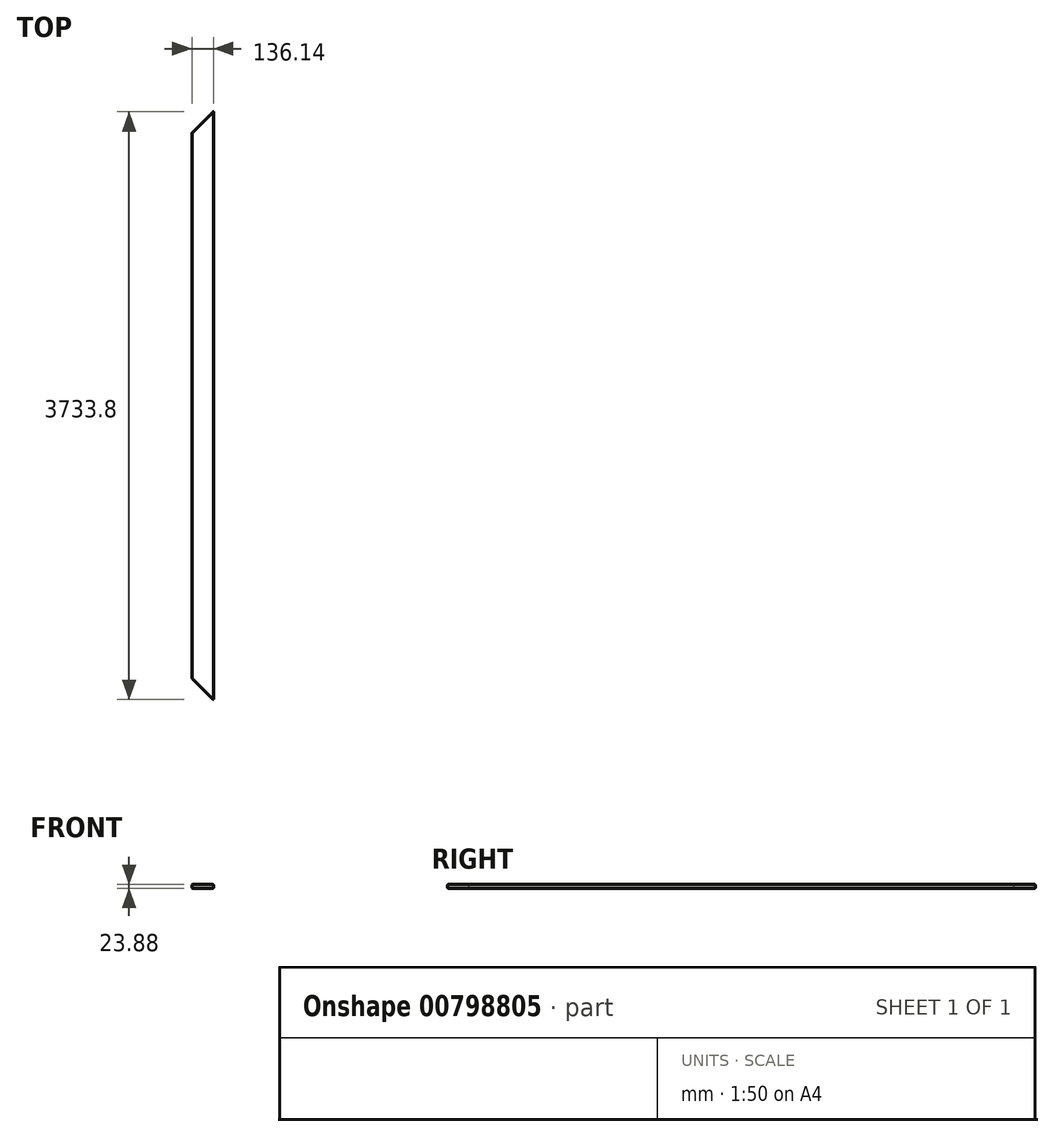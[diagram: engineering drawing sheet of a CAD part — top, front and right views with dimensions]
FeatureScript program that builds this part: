
annotation { "Feature Type Name" : "Feature", "Feature Type Description" : "" }
export const myFeature = defineFeature(function(context is Context, id is Id, definition is map)
    precondition{}
    {
        {
            var Q0;
            Q0=qCreatedBy(makeId("Front.planeOp"),FACE);
            var sketch = newSketch(context, id + "F0", { "sketchPlane" : qUnion([Q0])});
            skLineSegment(sketch, "E0.bottom", {"start": v(-63.25, 11.94) * mm, "end": v(63.25, 11.94) * mm});
            skLineSegment(sketch, "E0.top", {"start": v(-63.25, -11.94) * mm, "end": v(63.25, -11.94) * mm});
            skLineSegment(sketch, "E0.left", {"start": v(-68.07, 7.11) * mm, "end": v(-68.07, -7.11) * mm});
            skLineSegment(sketch, "E0.right", {"start": v(68.07, 7.11) * mm, "end": v(68.07, -7.11) * mm});
            skPoint(sketch, "E0.middle", {"position": v(0, 0) * mm});
            skPoint(sketch, "E1.visualSharp", {"position": v(-68.07, 11.94) * mm});
            skArc(sketch, "E1.filletArc", {"start": v(-63.25, 11.94) * mm, "mid": v(-66.66, 10.52) * mm, "end": v(-68.07, 7.11) * mm});
            skPoint(sketch, "E2.visualSharp", {"position": v(68.07, 11.94) * mm});
            skArc(sketch, "E2.filletArc", {"start": v(68.07, 7.11) * mm, "mid": v(66.66, 10.52) * mm, "end": v(63.25, 11.94) * mm});
            skPoint(sketch, "E3.visualSharp", {"position": v(68.07, -11.94) * mm});
            skArc(sketch, "E3.filletArc", {"start": v(63.25, -11.94) * mm, "mid": v(66.66, -10.52) * mm, "end": v(68.07, -7.11) * mm});
            skPoint(sketch, "E4.visualSharp", {"position": v(-68.07, -11.94) * mm});
            skArc(sketch, "E4.filletArc", {"start": v(-68.07, -7.11) * mm, "mid": v(-66.66, -10.52) * mm, "end": v(-63.25, -11.94) * mm});
            skSolve(sketch);
        }
        {
            var Q0;
            Q0=makeQuery(id+"F0.imprint","IMPRINT",FACE,{"disambiguationData":[TD([[makeQuery(id+"F0.imprint","IMPRINT",EDGE,{"derivedFrom":sQuery(id+"F0.wireOp",EDGE,"E0.bottom")}),-1.0]])]});
            extrude(context, id + "F1", {"entities" : qUnion([Q0]), "endBound" : BoundingType.SYMMETRIC, "depth" : 3733.8 * mm, "offsetDistance" : 25.4 * mm});
        }
        {
            var Q0;
            Q0=makeQuery(id+"F1.opExtrude","SWEPT_FACE",FACE,{"disambiguationData":[OSD([sQuery(id+"F0.wireOp",EDGE,"E0.bottom")])]});
            var sketch = newSketch(context, id + "F2", { "sketchPlane" : qUnion([Q0])});
            skLineSegment(sketch, "E5", {"start": v(-68.07, -1730.76) * mm, "end": v(-68.07, -1866.9) * mm});
            skLineSegment(sketch, "E6", {"start": v(68.07, -1866.9) * mm, "end": v(-68.07, -1866.9) * mm});
            skLineSegment(sketch, "E7", {"start": v(-68.07, -1730.76) * mm, "end": v(68.07, -1866.9) * mm});
            skLineSegment(sketch, "E8.MirrorCS", {"start": v(-68.07, 1730.76) * mm, "end": v(-68.07, 1866.9) * mm});
            skLineSegment(sketch, "E9.MirrorCS", {"start": v(68.07, 1866.9) * mm, "end": v(-68.07, 1866.9) * mm});
            skLineSegment(sketch, "E10.MirrorCS", {"start": v(-68.07, 1730.76) * mm, "end": v(68.07, 1866.9) * mm});
            skSolve(sketch);
        }
        {
            var Q0;
            Q0 = qSketchRegion(id + "F2", true);
            extrude(context, id + "F3", {"entities" : qUnion([Q0]), "operationType" : NewBodyOperationType.REMOVE, "endBound" : BoundingType.THROUGH_ALL, "oppositeDirection" : true, "depth" : 25.4 * mm, "offsetDistance" : 25.4 * mm});
        }
    });
